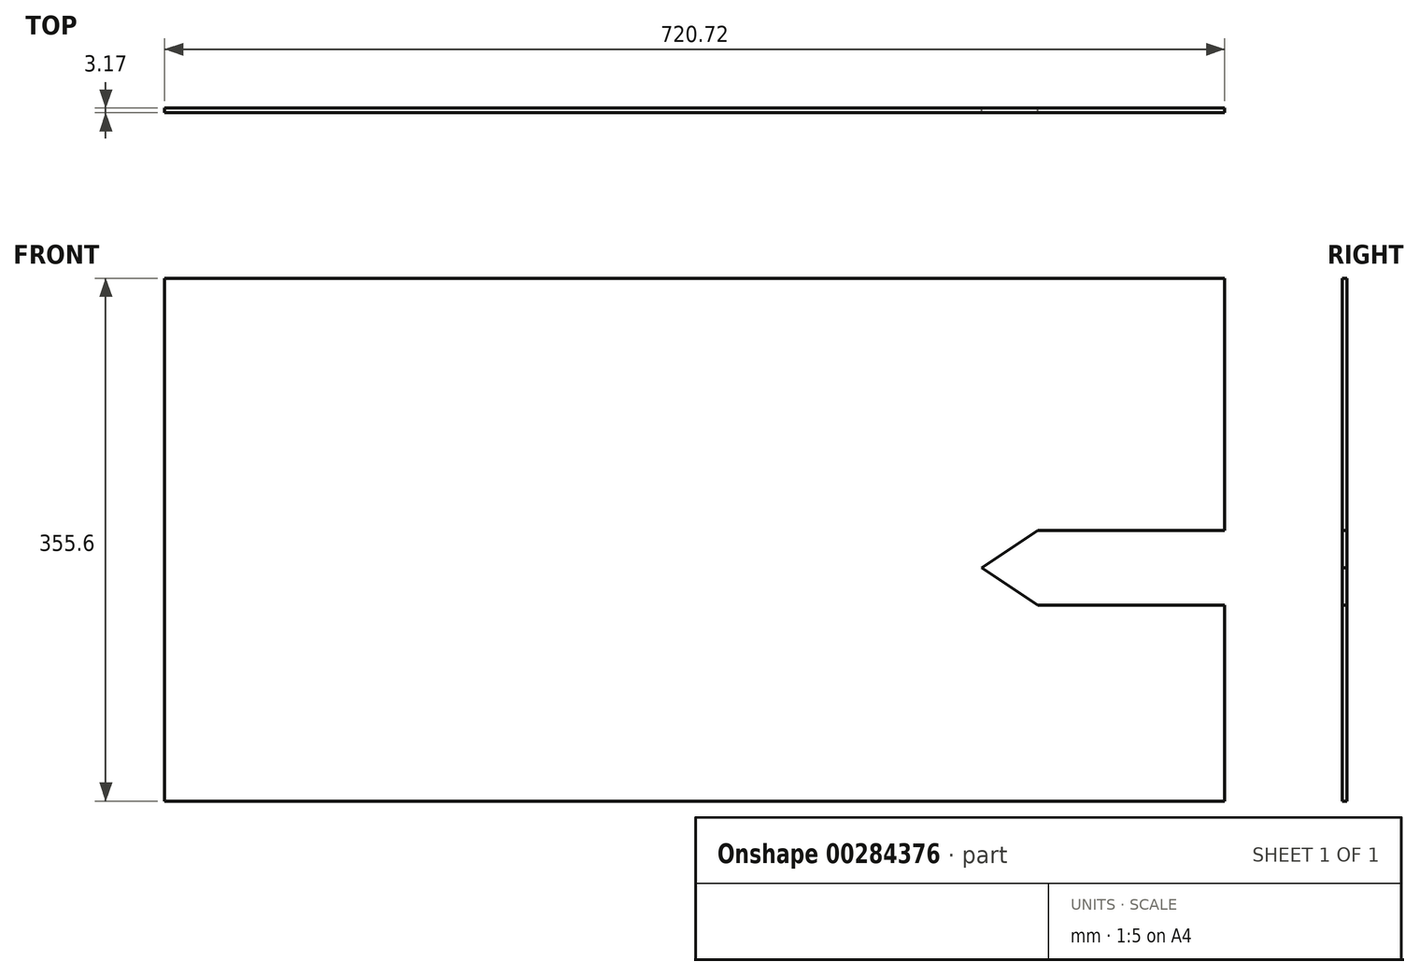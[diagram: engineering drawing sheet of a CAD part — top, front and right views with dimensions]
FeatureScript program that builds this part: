
annotation { "Feature Type Name" : "Feature", "Feature Type Description" : "" }
export const myFeature = defineFeature(function(context is Context, id is Id, definition is map)
    precondition{}
    {
        {
            var Q0;
            Q0=qCreatedBy(makeId("Front.planeOp"),FACE);
            var sketch = newSketch(context, id + "F0", { "sketchPlane" : qUnion([Q0])});
            skLineSegment(sketch, "E0", {"start": v(0, 0) * mm, "end": v(0, 355.6) * mm});
            skLineSegment(sketch, "E1", {"start": v(0, 355.6) * mm, "end": v(720.73, 355.6) * mm});
            skLineSegment(sketch, "E2", {"start": v(720.73, 355.6) * mm, "end": v(720.73, 184.15) * mm});
            skLineSegment(sketch, "E3", {"start": v(720.73, 184.15) * mm, "end": v(593.73, 184.15) * mm});
            skLineSegment(sketch, "E4", {"start": v(593.73, 184.15) * mm, "end": v(555.63, 158.75) * mm});
            skLineSegment(sketch, "E5", {"start": v(555.63, 158.75) * mm, "end": v(593.73, 133.35) * mm});
            skLineSegment(sketch, "E6", {"start": v(593.73, 133.35) * mm, "end": v(720.73, 133.35) * mm});
            skLineSegment(sketch, "E7", {"start": v(720.73, 133.35) * mm, "end": v(720.73, 0) * mm});
            skLineSegment(sketch, "E8", {"start": v(720.73, 0) * mm, "end": v(0, 0) * mm});
            skSolve(sketch);
        }
        {
            var Q0;
            Q0=makeQuery(id+"F0.imprint","IMPRINT",FACE,{"disambiguationData":[TD([[makeQuery(id+"F0.imprint","IMPRINT",EDGE,{"derivedFrom":sQuery(id+"F0.wireOp",EDGE,"E0")}),-1.0]])]});
            extrude(context, id + "F1", {"entities" : qUnion([Q0]), "depth" : 3.17 * mm});
        }
    });
